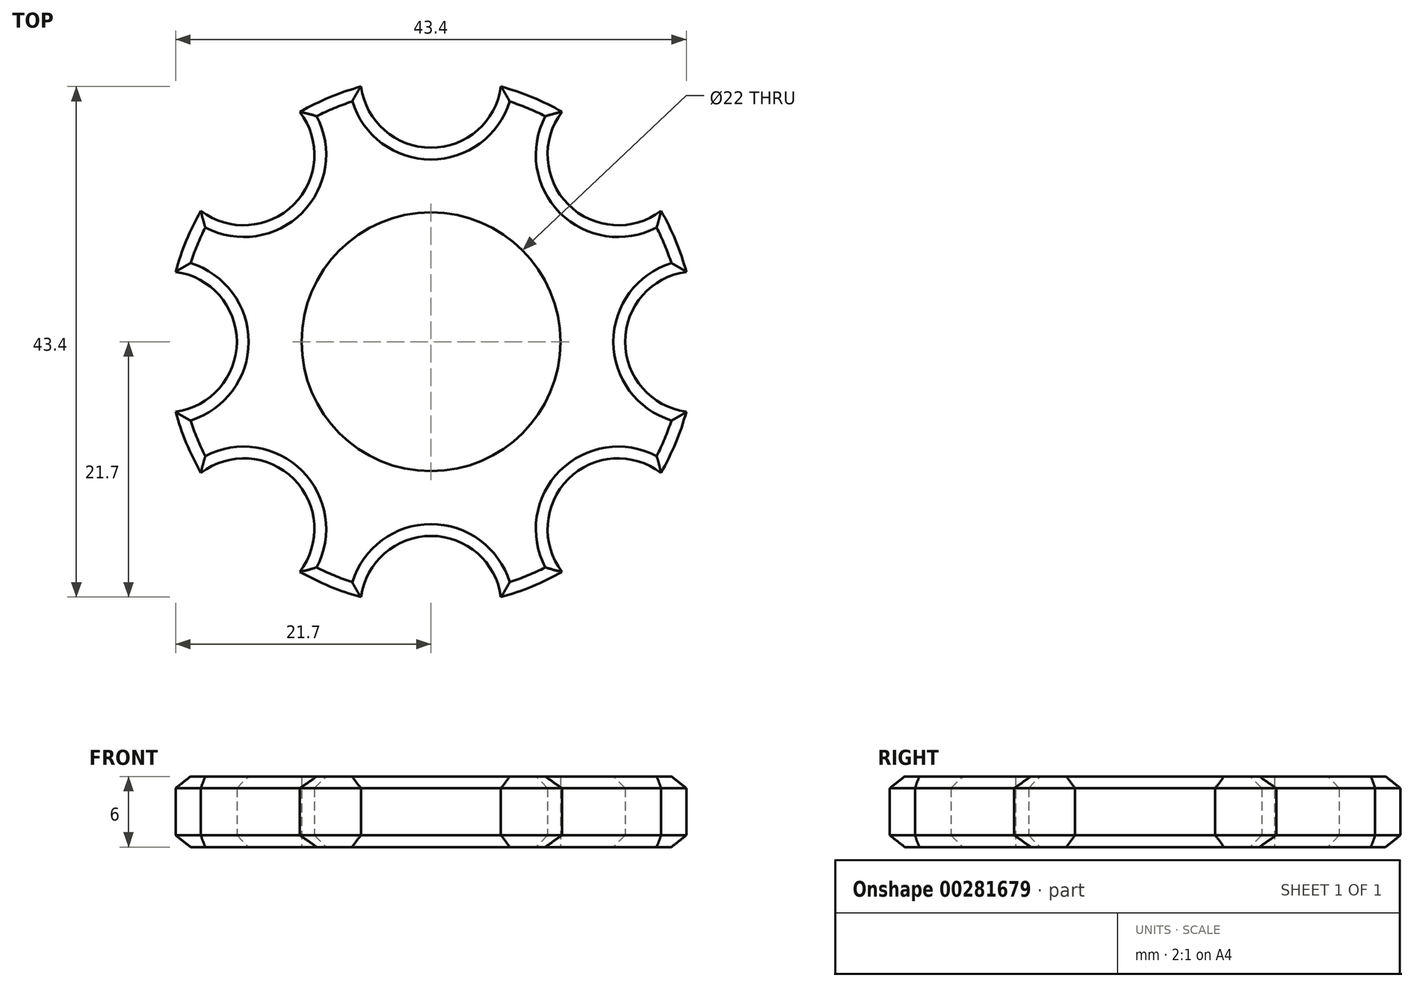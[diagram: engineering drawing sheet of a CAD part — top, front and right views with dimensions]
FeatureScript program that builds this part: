
annotation { "Feature Type Name" : "Feature", "Feature Type Description" : "" }
export const myFeature = defineFeature(function(context is Context, id is Id, definition is map)
    precondition{}
    {
        {
            var Q0;
            Q0=qCreatedBy(makeId("Top.planeOp"),FACE);
            var sketch = newSketch(context, id + "F0", { "sketchPlane" : qUnion([Q0])});
            skCircle(sketch, "E0", {"center": v(0, 0) * mm, "radius": 11 * mm});
            skArc(sketch, "E1", {"start": v(-19.55, 11.14) * mm, "mid": v(-20.79, 8.61) * mm, "end": v(-21.7, 5.95) * mm});
            skArc(sketch, "E2", {"start": v(-5.95, 21.7) * mm, "mid": v(0, 16.5) * mm, "end": v(5.95, 21.7) * mm});
            skArc(sketch, "E3.1.0", {"start": v(-19.55, 11.14) * mm, "mid": v(-11.67, 11.67) * mm, "end": v(-11.14, 19.55) * mm});
            skArc(sketch, "E3.2.0", {"start": v(-21.7, -5.95) * mm, "mid": v(-16.5, 0) * mm, "end": v(-21.7, 5.95) * mm});
            skArc(sketch, "E3.3.0", {"start": v(-11.14, -19.55) * mm, "mid": v(-11.67, -11.67) * mm, "end": v(-19.55, -11.14) * mm});
            skArc(sketch, "E3.4.0", {"start": v(5.95, -21.7) * mm, "mid": v(0, -16.5) * mm, "end": v(-5.95, -21.7) * mm});
            skArc(sketch, "E3.5.0", {"start": v(19.55, -11.14) * mm, "mid": v(11.67, -11.67) * mm, "end": v(11.14, -19.55) * mm});
            skArc(sketch, "E3.6.0", {"start": v(21.7, 5.95) * mm, "mid": v(16.5, 0) * mm, "end": v(21.7, -5.95) * mm});
            skArc(sketch, "E3.7.0", {"start": v(11.14, 19.55) * mm, "mid": v(11.67, 11.67) * mm, "end": v(19.55, 11.14) * mm});
            skArc(sketch, "E4.trimOffspring", {"start": v(-5.95, 21.7) * mm, "mid": v(-8.61, 20.79) * mm, "end": v(-11.14, 19.55) * mm});
            skArc(sketch, "E5.trimOffspring", {"start": v(11.14, 19.55) * mm, "mid": v(8.61, 20.79) * mm, "end": v(5.95, 21.7) * mm});
            skArc(sketch, "E6.trimOffspring", {"start": v(21.7, 5.95) * mm, "mid": v(20.79, 8.61) * mm, "end": v(19.55, 11.14) * mm});
            skArc(sketch, "E7.trimOffspring", {"start": v(-21.7, -5.95) * mm, "mid": v(-20.79, -8.61) * mm, "end": v(-19.55, -11.14) * mm});
            skArc(sketch, "E8.trimOffspring", {"start": v(-11.14, -19.55) * mm, "mid": v(-8.61, -20.79) * mm, "end": v(-5.95, -21.7) * mm});
            skArc(sketch, "E9.trimOffspring", {"start": v(5.95, -21.7) * mm, "mid": v(8.61, -20.79) * mm, "end": v(11.14, -19.55) * mm});
            skArc(sketch, "E10.trimOffspring", {"start": v(19.55, -11.14) * mm, "mid": v(20.79, -8.61) * mm, "end": v(21.7, -5.95) * mm});
            skSolve(sketch);
        }
        {
            var Q0;
            Q0=makeQuery(id+"F0.imprint","IMPRINT",FACE,{"disambiguationData":[TD([[makeQuery(id+"F0.imprint","IMPRINT",EDGE,{"derivedFrom":sQuery(id+"F0.wireOp",EDGE,"E0")}),-1.0]])]});
            extrude(context, id + "F1", {"entities" : qUnion([Q0]), "depth" : 6 * mm});
        }
        {
            var Q0;
            Q0=makeQuery(id+"F1.opExtrude","CAP_EDGE",EDGE,{"disambiguationData":[OSD([sQuery(id+"F0.wireOp",EDGE,"E3.2.0")])],"isStart":true});
            var Q1;
            Q1=makeQuery(id+"F1.opExtrude","CAP_EDGE",EDGE,{"disambiguationData":[OSD([sQuery(id+"F0.wireOp",EDGE,"E1")])],"isStart":true});
            var Q2;
            Q2=makeQuery(id+"F1.opExtrude","CAP_EDGE",EDGE,{"disambiguationData":[OSD([sQuery(id+"F0.wireOp",EDGE,"E3.1.0")])],"isStart":true});
            var Q3;
            Q3=makeQuery(id+"F1.opExtrude","CAP_EDGE",EDGE,{"disambiguationData":[OSD([sQuery(id+"F0.wireOp",EDGE,"E4.trimOffspring")])],"isStart":true});
            var Q4;
            Q4=makeQuery(id+"F1.opExtrude","CAP_EDGE",EDGE,{"disambiguationData":[OSD([sQuery(id+"F0.wireOp",EDGE,"E2")])],"isStart":true});
            var Q5;
            Q5=makeQuery(id+"F1.opExtrude","CAP_EDGE",EDGE,{"disambiguationData":[OSD([sQuery(id+"F0.wireOp",EDGE,"E5.trimOffspring")])],"isStart":true});
            var Q6;
            Q6=makeQuery(id+"F1.opExtrude","CAP_EDGE",EDGE,{"disambiguationData":[OSD([sQuery(id+"F0.wireOp",EDGE,"E3.7.0")])],"isStart":true});
            var Q7;
            Q7=makeQuery(id+"F1.opExtrude","CAP_EDGE",EDGE,{"disambiguationData":[OSD([sQuery(id+"F0.wireOp",EDGE,"E6.trimOffspring")])],"isStart":true});
            var Q8;
            Q8=makeQuery(id+"F1.opExtrude","CAP_EDGE",EDGE,{"disambiguationData":[OSD([sQuery(id+"F0.wireOp",EDGE,"E3.6.0")])],"isStart":true});
            var Q9;
            Q9=makeQuery(id+"F1.opExtrude","CAP_EDGE",EDGE,{"disambiguationData":[OSD([sQuery(id+"F0.wireOp",EDGE,"E3.5.0")])],"isStart":true});
            var Q10;
            Q10=makeQuery(id+"F1.opExtrude","CAP_EDGE",EDGE,{"disambiguationData":[OSD([sQuery(id+"F0.wireOp",EDGE,"E10.trimOffspring")])],"isStart":true});
            var Q11;
            Q11=makeQuery(id+"F1.opExtrude","CAP_EDGE",EDGE,{"disambiguationData":[OSD([sQuery(id+"F0.wireOp",EDGE,"E9.trimOffspring")])],"isStart":true});
            var Q12;
            Q12=makeQuery(id+"F1.opExtrude","CAP_EDGE",EDGE,{"disambiguationData":[OSD([sQuery(id+"F0.wireOp",EDGE,"E3.4.0")])],"isStart":true});
            var Q13;
            Q13=makeQuery(id+"F1.opExtrude","CAP_EDGE",EDGE,{"disambiguationData":[OSD([sQuery(id+"F0.wireOp",EDGE,"E8.trimOffspring")])],"isStart":true});
            var Q14;
            Q14=makeQuery(id+"F1.opExtrude","CAP_EDGE",EDGE,{"disambiguationData":[OSD([sQuery(id+"F0.wireOp",EDGE,"E3.3.0")])],"isStart":true});
            var Q15;
            Q15=makeQuery(id+"F1.opExtrude","CAP_EDGE",EDGE,{"disambiguationData":[OSD([sQuery(id+"F0.wireOp",EDGE,"E7.trimOffspring")])],"isStart":true});
            var Q16;
            Q16=makeQuery(id+"F1.opExtrude","CAP_EDGE",EDGE,{"disambiguationData":[OSD([sQuery(id+"F0.wireOp",EDGE,"E2")])],"isStart":false});
            var Q17;
            Q17=makeQuery(id+"F1.opExtrude","CAP_EDGE",EDGE,{"disambiguationData":[OSD([sQuery(id+"F0.wireOp",EDGE,"E3.1.0")])],"isStart":false});
            var Q18;
            Q18=makeQuery(id+"F1.opExtrude","CAP_EDGE",EDGE,{"disambiguationData":[OSD([sQuery(id+"F0.wireOp",EDGE,"E4.trimOffspring")])],"isStart":false});
            var Q19;
            Q19=makeQuery(id+"F1.opExtrude","CAP_EDGE",EDGE,{"disambiguationData":[OSD([sQuery(id+"F0.wireOp",EDGE,"E5.trimOffspring")])],"isStart":false});
            var Q20;
            Q20=makeQuery(id+"F1.opExtrude","CAP_EDGE",EDGE,{"disambiguationData":[OSD([sQuery(id+"F0.wireOp",EDGE,"E3.7.0")])],"isStart":false});
            var Q21;
            Q21=makeQuery(id+"F1.opExtrude","CAP_EDGE",EDGE,{"disambiguationData":[OSD([sQuery(id+"F0.wireOp",EDGE,"E6.trimOffspring")])],"isStart":false});
            var Q22;
            Q22=makeQuery(id+"F1.opExtrude","CAP_EDGE",EDGE,{"disambiguationData":[OSD([sQuery(id+"F0.wireOp",EDGE,"E3.6.0")])],"isStart":false});
            var Q23;
            Q23=makeQuery(id+"F1.opExtrude","CAP_EDGE",EDGE,{"disambiguationData":[OSD([sQuery(id+"F0.wireOp",EDGE,"E10.trimOffspring")])],"isStart":false});
            var Q24;
            Q24=makeQuery(id+"F1.opExtrude","CAP_EDGE",EDGE,{"disambiguationData":[OSD([sQuery(id+"F0.wireOp",EDGE,"E3.5.0")])],"isStart":false});
            var Q25;
            Q25=makeQuery(id+"F1.opExtrude","CAP_EDGE",EDGE,{"disambiguationData":[OSD([sQuery(id+"F0.wireOp",EDGE,"E3.4.0")])],"isStart":false});
            var Q26;
            Q26=makeQuery(id+"F1.opExtrude","CAP_EDGE",EDGE,{"disambiguationData":[OSD([sQuery(id+"F0.wireOp",EDGE,"E9.trimOffspring")])],"isStart":false});
            var Q27;
            Q27=makeQuery(id+"F1.opExtrude","CAP_EDGE",EDGE,{"disambiguationData":[OSD([sQuery(id+"F0.wireOp",EDGE,"E8.trimOffspring")])],"isStart":false});
            var Q28;
            Q28=makeQuery(id+"F1.opExtrude","CAP_EDGE",EDGE,{"disambiguationData":[OSD([sQuery(id+"F0.wireOp",EDGE,"E3.3.0")])],"isStart":false});
            var Q29;
            Q29=makeQuery(id+"F1.opExtrude","CAP_EDGE",EDGE,{"disambiguationData":[OSD([sQuery(id+"F0.wireOp",EDGE,"E7.trimOffspring")])],"isStart":false});
            var Q30;
            Q30=makeQuery(id+"F1.opExtrude","CAP_EDGE",EDGE,{"disambiguationData":[OSD([sQuery(id+"F0.wireOp",EDGE,"E3.2.0")])],"isStart":false});
            var Q31;
            Q31=makeQuery(id+"F1.opExtrude","CAP_EDGE",EDGE,{"disambiguationData":[OSD([sQuery(id+"F0.wireOp",EDGE,"E1")])],"isStart":false});
            chamfer(context, id + "F2", {"entities" : qUnion([Q0, Q1, Q2, Q3, Q4, Q5, Q6, Q7, Q8, Q9, Q10, Q11, Q12, Q13, Q14, Q15, Q16, Q17, Q18, Q19, Q20, Q21, Q22, Q23, Q24, Q25, Q26, Q27, Q28, Q29, Q30, Q31]), "width" : 1 * mm, "tangentPropagation" : true});
        }
    });
